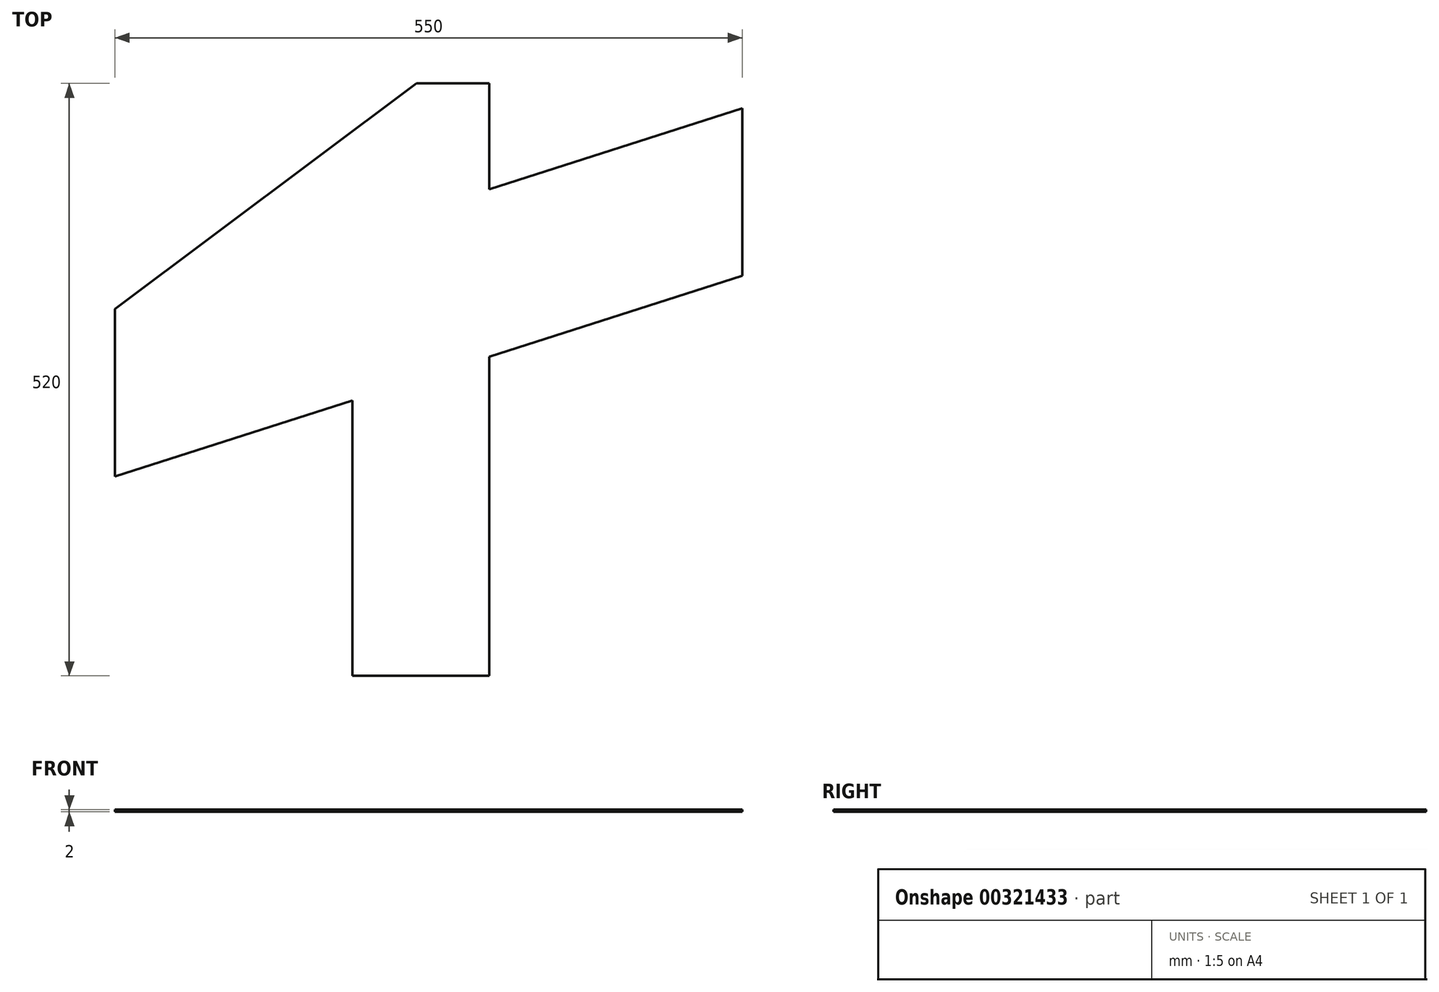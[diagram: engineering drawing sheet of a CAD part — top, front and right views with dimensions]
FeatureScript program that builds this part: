
annotation { "Feature Type Name" : "Feature", "Feature Type Description" : "" }
export const myFeature = defineFeature(function(context is Context, id is Id, definition is map)
    precondition{}
    {
        {
            var Q0;
            Q0=qCreatedBy(makeId("Top.planeOp"),FACE);
            var sketch = newSketch(context, id + "F0", { "sketchPlane" : qUnion([Q0])});
            skLineSegment(sketch, "E0.bottom", {"start": v(275, 260) * mm, "end": v(53.23, 260) * mm, "construction": true});
            skLineSegment(sketch, "E0.top", {"start": v(275, -260) * mm, "end": v(-275, -260) * mm, "construction": true});
            skLineSegment(sketch, "E0.left", {"start": v(275, 260) * mm, "end": v(275, 238) * mm, "construction": true});
            skLineSegment(sketch, "E0.right", {"start": v(-275, 260) * mm, "end": v(-275, 61.91) * mm, "construction": true});
            skPoint(sketch, "E0.middle", {"position": v(0, 0) * mm});
            skLineSegment(sketch, "E1", {"start": v(-275, -85.09) * mm, "end": v(-66.77, -18.42) * mm});
            skLineSegment(sketch, "E2", {"start": v(275, 238) * mm, "end": v(53.23, 167) * mm});
            skLineSegment(sketch, "E3", {"start": v(275, 238) * mm, "end": v(275, 91) * mm, "construction": true});
            skLineSegment(sketch, "E4", {"start": v(53.23, -260) * mm, "end": v(53.23, 20) * mm});
            skLineSegment(sketch, "E5", {"start": v(53.23, 167) * mm, "end": v(53.23, 260) * mm});
            skLineSegment(sketch, "E6", {"start": v(53.23, 20) * mm, "end": v(53.23, 167) * mm, "construction": true});
            skLineSegment(sketch, "E7", {"start": v(-66.77, 260) * mm, "end": v(-66.77, 218.02) * mm, "construction": true});
            skLineSegment(sketch, "E8", {"start": v(-66.77, 128.58) * mm, "end": v(-66.77, -18.42) * mm, "construction": true});
            skLineSegment(sketch, "E9", {"start": v(-66.77, -18.42) * mm, "end": v(-66.77, -260) * mm});
            skLineSegment(sketch, "E10", {"start": v(-275, 61.91) * mm, "end": v(-10.77, 260) * mm});
            skLineSegment(sketch, "E11", {"start": v(-66.77, 218.02) * mm, "end": v(-66.77, 128.58) * mm, "construction": true});
            skLineSegment(sketch, "E12", {"start": v(53.23, 167) * mm, "end": v(-275, 61.91) * mm, "construction": true});
            skLineSegment(sketch, "E13", {"start": v(-275, -85.09) * mm, "end": v(-275, -260) * mm, "construction": true});
            skLineSegment(sketch, "E14", {"start": v(-275, 61.91) * mm, "end": v(-275, -85.09) * mm, "construction": true});
            skLineSegment(sketch, "E15", {"start": v(-10.77, 260) * mm, "end": v(-275, 260) * mm, "construction": true});
            skLineSegment(sketch, "E16", {"start": v(275, 91) * mm, "end": v(275, -260) * mm, "construction": true});
            skLineSegment(sketch, "E17", {"start": v(-66.77, -18.42) * mm, "end": v(53.23, 20) * mm, "construction": true});
            skLineSegment(sketch, "E18", {"start": v(53.23, 20) * mm, "end": v(53.23, 20) * mm});
            skLineSegment(sketch, "E19", {"start": v(53.23, 20) * mm, "end": v(275, 91) * mm});
            skLineSegment(sketch, "E20", {"start": v(-275, 61.91) * mm, "end": v(-275, -85.09) * mm});
            skLineSegment(sketch, "E21", {"start": v(-66.77, -260) * mm, "end": v(53.23, -260) * mm});
            skLineSegment(sketch, "E22", {"start": v(275, 238) * mm, "end": v(275, 91) * mm});
            skLineSegment(sketch, "E23", {"start": v(-10.77, 260) * mm, "end": v(53.23, 260) * mm});
            skLineSegment(sketch, "E24", {"start": v(-275, 61.91) * mm, "end": v(275, 61.91) * mm, "construction": true});
            skSolve(sketch);
        }
        {
            var Q0;
            Q0 = qSketchRegion(id + "F0", true);
            extrude(context, id + "F1", {"entities" : qUnion([Q0]), "depth" : 2 * mm});
        }
    });
